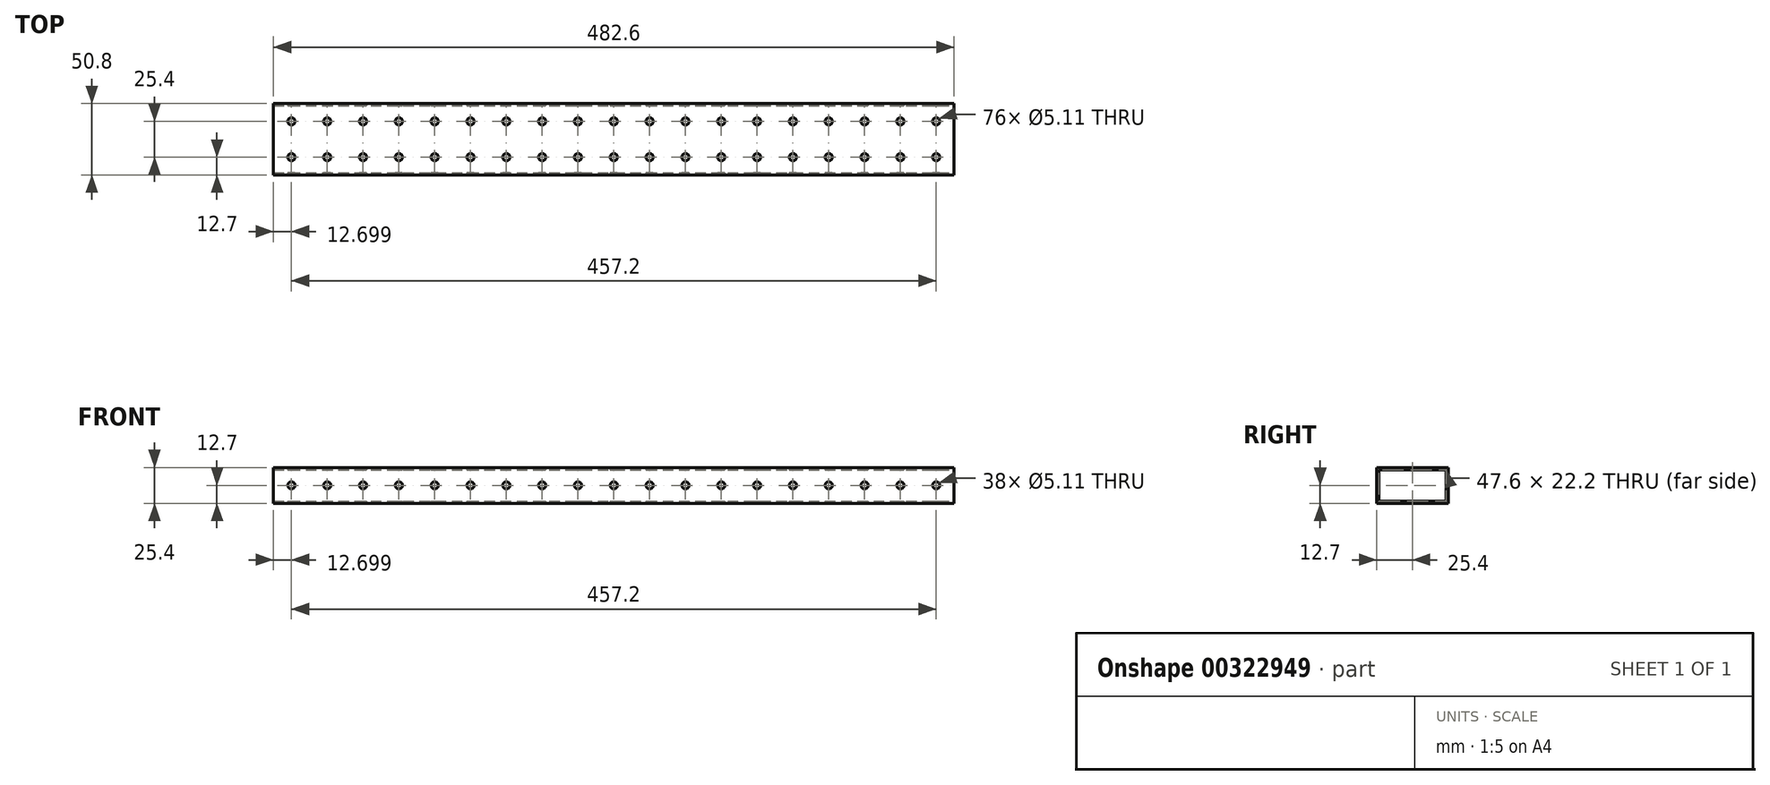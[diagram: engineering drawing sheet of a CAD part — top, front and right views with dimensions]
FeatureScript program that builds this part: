
annotation { "Feature Type Name" : "Feature", "Feature Type Description" : "" }
export const myFeature = defineFeature(function(context is Context, id is Id, definition is map)
    precondition{}
    {
        {
            var Q0;
            Q0=qCreatedBy(makeId("Top.planeOp"),FACE);
            var sketch = newSketch(context, id + "F0", { "sketchPlane" : qUnion([Q0])});
            skLineSegment(sketch, "E0.bottom", {"start": v(-213.03, 43.97) * mm, "end": v(269.57, 43.97) * mm});
            skLineSegment(sketch, "E0.top", {"start": v(-213.03, -6.83) * mm, "end": v(269.57, -6.83) * mm});
            skLineSegment(sketch, "E0.left", {"start": v(-213.03, 43.97) * mm, "end": v(-213.03, -6.83) * mm});
            skLineSegment(sketch, "E0.right", {"start": v(269.57, 43.97) * mm, "end": v(269.57, -6.83) * mm});
            skSolve(sketch);
        }
        {
            var Q0;
            Q0=makeQuery(id+"F0.imprint","IMPRINT",FACE,{"disambiguationData":[TD([[makeQuery(id+"F0.imprint","IMPRINT",EDGE,{"derivedFrom":sQuery(id+"F0.wireOp",EDGE,"E0.bottom")}),-1.0]])]});
            extrude(context, id + "F1", {"entities" : qUnion([Q0]), "depth" : 25.4 * mm});
        }
        {
            var Q0;
            Q0=makeQuery(id+"F1.opExtrude","SWEPT_FACE",FACE,{"disambiguationData":[OSD([sQuery(id+"F0.wireOp",EDGE,"E0.right")])]});
            var sketch = newSketch(context, id + "F2", { "sketchPlane" : qUnion([Q0])});
            skLineSegment(sketch, "E1.bottom", {"start": v(-5.23, 23.8) * mm, "end": v(42.37, 23.8) * mm});
            skLineSegment(sketch, "E1.top", {"start": v(-5.23, 1.6) * mm, "end": v(42.37, 1.6) * mm});
            skLineSegment(sketch, "E1.left", {"start": v(-5.23, 23.8) * mm, "end": v(-5.23, 1.6) * mm});
            skLineSegment(sketch, "E1.right", {"start": v(42.37, 23.8) * mm, "end": v(42.37, 1.6) * mm});
            skSolve(sketch);
        }
        {
            var Q0;
            Q0 = qSketchRegion(id + "F2", true);
            extrude(context, id + "F3", {"entities" : qUnion([Q0]), "operationType" : NewBodyOperationType.REMOVE, "endBound" : BoundingType.THROUGH_ALL, "oppositeDirection" : true, "depth" : 25.4 * mm});
        }
        {
            var Q0;
            Q0=makeQuery(id+"F1.opExtrude","CAP_FACE",FACE,{"disambiguationData":[OSD([sQuery(id+"F0.wireOp",EDGE,"E0.bottom"),sQuery(id+"F0.wireOp",EDGE,"E0.top"),sQuery(id+"F0.wireOp",EDGE,"E0.left"),sQuery(id+"F0.wireOp",EDGE,"E0.right")])],"isStart":false});
            var sketch = newSketch(context, id + "F4", { "sketchPlane" : qUnion([Q0])});
            skCircle(sketch, "E2", {"center": v(-200.33, 31.27) * mm, "radius": 2.55 * mm});
            skCircle(sketch, "E3.0.1.0", {"center": v(-200.33, 5.87) * mm, "radius": 2.55 * mm});
            skCircle(sketch, "E3.1.0.0", {"center": v(-174.93, 31.27) * mm, "radius": 2.55 * mm});
            skCircle(sketch, "E3.1.1.0", {"center": v(-174.93, 5.87) * mm, "radius": 2.55 * mm});
            skCircle(sketch, "E3.2.0.0", {"center": v(-149.53, 31.27) * mm, "radius": 2.55 * mm});
            skCircle(sketch, "E3.2.1.0", {"center": v(-149.53, 5.87) * mm, "radius": 2.55 * mm});
            skCircle(sketch, "E3.3.0.0", {"center": v(-124.13, 31.27) * mm, "radius": 2.55 * mm});
            skCircle(sketch, "E3.3.1.0", {"center": v(-124.13, 5.87) * mm, "radius": 2.55 * mm});
            skCircle(sketch, "E3.4.0.0", {"center": v(-98.73, 31.27) * mm, "radius": 2.55 * mm});
            skCircle(sketch, "E3.4.1.0", {"center": v(-98.73, 5.87) * mm, "radius": 2.55 * mm});
            skCircle(sketch, "E3.5.0.0", {"center": v(-73.33, 31.27) * mm, "radius": 2.55 * mm});
            skCircle(sketch, "E3.5.1.0", {"center": v(-73.33, 5.87) * mm, "radius": 2.55 * mm});
            skCircle(sketch, "E3.6.0.0", {"center": v(-47.93, 31.27) * mm, "radius": 2.55 * mm});
            skCircle(sketch, "E3.6.1.0", {"center": v(-47.93, 5.87) * mm, "radius": 2.55 * mm});
            skCircle(sketch, "E3.7.0.0", {"center": v(-22.53, 31.27) * mm, "radius": 2.55 * mm});
            skCircle(sketch, "E3.7.1.0", {"center": v(-22.53, 5.87) * mm, "radius": 2.55 * mm});
            skCircle(sketch, "E3.8.0.0", {"center": v(2.87, 31.27) * mm, "radius": 2.55 * mm});
            skCircle(sketch, "E3.8.1.0", {"center": v(2.87, 5.87) * mm, "radius": 2.55 * mm});
            skCircle(sketch, "E3.9.0.0", {"center": v(28.27, 31.27) * mm, "radius": 2.55 * mm});
            skCircle(sketch, "E3.9.1.0", {"center": v(28.27, 5.87) * mm, "radius": 2.55 * mm});
            skCircle(sketch, "E3.10.0.0", {"center": v(53.67, 31.27) * mm, "radius": 2.55 * mm});
            skCircle(sketch, "E3.10.1.0", {"center": v(53.67, 5.87) * mm, "radius": 2.55 * mm});
            skCircle(sketch, "E3.11.0.0", {"center": v(79.07, 31.27) * mm, "radius": 2.55 * mm});
            skCircle(sketch, "E3.11.1.0", {"center": v(79.07, 5.87) * mm, "radius": 2.55 * mm});
            skCircle(sketch, "E3.12.0.0", {"center": v(104.47, 31.27) * mm, "radius": 2.55 * mm});
            skCircle(sketch, "E3.12.1.0", {"center": v(104.47, 5.87) * mm, "radius": 2.55 * mm});
            skCircle(sketch, "E3.13.0.0", {"center": v(129.87, 31.27) * mm, "radius": 2.55 * mm});
            skCircle(sketch, "E3.13.1.0", {"center": v(129.87, 5.87) * mm, "radius": 2.55 * mm});
            skCircle(sketch, "E3.14.0.0", {"center": v(155.27, 31.27) * mm, "radius": 2.55 * mm});
            skCircle(sketch, "E3.14.1.0", {"center": v(155.27, 5.87) * mm, "radius": 2.55 * mm});
            skCircle(sketch, "E3.15.0.0", {"center": v(180.67, 31.27) * mm, "radius": 2.55 * mm});
            skCircle(sketch, "E3.15.1.0", {"center": v(180.67, 5.87) * mm, "radius": 2.55 * mm});
            skCircle(sketch, "E3.16.0.0", {"center": v(206.07, 31.27) * mm, "radius": 2.55 * mm});
            skCircle(sketch, "E3.16.1.0", {"center": v(206.07, 5.87) * mm, "radius": 2.55 * mm});
            skCircle(sketch, "E3.17.0.0", {"center": v(231.47, 31.27) * mm, "radius": 2.55 * mm});
            skCircle(sketch, "E3.17.1.0", {"center": v(231.47, 5.87) * mm, "radius": 2.55 * mm});
            skCircle(sketch, "E3.18.0.0", {"center": v(256.87, 31.27) * mm, "radius": 2.55 * mm});
            skCircle(sketch, "E3.18.1.0", {"center": v(256.87, 5.87) * mm, "radius": 2.55 * mm});
            skLineSegment(sketch, "E3.direction1", {"start": v(-200.33, 31.27) * mm, "end": v(-174.93, 31.27) * mm, "construction": true});
            skLineSegment(sketch, "E3.direction2", {"start": v(-200.33, 31.27) * mm, "end": v(-200.33, 5.87) * mm, "construction": true});
            skSolve(sketch);
        }
        {
            var Q0;
            Q0=sQuery(id+"F4.wireOp",VERTEX,"E3.8.1.0.center");
            var Q1;
            Q1=sQuery(id+"F4.wireOp",VERTEX,"E3.6.0.0.center");
            var Q2;
            Q2=sQuery(id+"F4.wireOp",VERTEX,"E3.4.0.0.center");
            var Q3;
            Q3=sQuery(id+"F4.wireOp",VERTEX,"E3.7.1.0.center");
            var Q4;
            Q4=sQuery(id+"F4.wireOp",VERTEX,"E3.3.1.0.center");
            var Q5;
            Q5=sQuery(id+"F4.wireOp",VERTEX,"E3.3.0.0.center");
            var Q6;
            Q6=sQuery(id+"F4.wireOp",VERTEX,"E3.2.1.0.center");
            var Q7;
            Q7=sQuery(id+"F4.wireOp",VERTEX,"E3.8.0.0.center");
            var Q8;
            Q8=sQuery(id+"F4.wireOp",VERTEX,"E3.2.0.0.center");
            var Q9;
            Q9=sQuery(id+"F4.wireOp",VERTEX,"E3.1.1.0.center");
            var Q10;
            Q10=sQuery(id+"F4.wireOp",VERTEX,"E3.1.0.0.center");
            var Q11;
            Q11=sQuery(id+"F4.wireOp",VERTEX,"E3.0.1.0.center");
            var Q12;
            Q12=sQuery(id+"F4.wireOp",VERTEX,"E2.center");
            var Q13;
            Q13=sQuery(id+"F4.wireOp",VERTEX,"E3.5.0.0.center");
            var Q14;
            Q14=sQuery(id+"F4.wireOp",VERTEX,"E3.5.1.0.center");
            var Q15;
            Q15=sQuery(id+"F4.wireOp",VERTEX,"E3.4.1.0.center");
            var Q16;
            Q16=sQuery(id+"F4.wireOp",VERTEX,"E3.7.0.0.center");
            var Q17;
            Q17=sQuery(id+"F4.wireOp",VERTEX,"E3.6.1.0.center");
            var Q18;
            Q18=sQuery(id+"F4.wireOp",VERTEX,"E3.18.0.0.center");
            var Q19;
            Q19=sQuery(id+"F4.wireOp",VERTEX,"E3.16.1.0.center");
            var Q20;
            Q20=sQuery(id+"F4.wireOp",VERTEX,"E3.13.0.0.center");
            var Q21;
            Q21=sQuery(id+"F4.wireOp",VERTEX,"E3.11.1.0.center");
            var Q22;
            Q22=sQuery(id+"F4.wireOp",VERTEX,"E3.14.0.0.center");
            var Q23;
            Q23=sQuery(id+"F4.wireOp",VERTEX,"E3.17.1.0.center");
            var Q24;
            Q24=sQuery(id+"F4.wireOp",VERTEX,"E3.15.1.0.center");
            var Q25;
            Q25=sQuery(id+"F4.wireOp",VERTEX,"E3.9.1.0.center");
            var Q26;
            Q26=sQuery(id+"F4.wireOp",VERTEX,"E3.18.1.0.center");
            var Q27;
            Q27=sQuery(id+"F4.wireOp",VERTEX,"E3.12.1.0.center");
            var Q28;
            Q28=sQuery(id+"F4.wireOp",VERTEX,"E3.10.1.0.center");
            var Q29;
            Q29=sQuery(id+"F4.wireOp",VERTEX,"E3.16.0.0.center");
            var Q30;
            Q30=sQuery(id+"F4.wireOp",VERTEX,"E3.15.0.0.center");
            var Q31;
            Q31=sQuery(id+"F4.wireOp",VERTEX,"E3.9.0.0.center");
            var Q32;
            Q32=sQuery(id+"F4.wireOp",VERTEX,"E3.13.1.0.center");
            var Q33;
            Q33=sQuery(id+"F4.wireOp",VERTEX,"E3.17.0.0.center");
            var Q34;
            Q34=sQuery(id+"F4.wireOp",VERTEX,"E3.10.0.0.center");
            var Q35;
            Q35=sQuery(id+"F4.wireOp",VERTEX,"E3.12.0.0.center");
            var Q36;
            Q36=sQuery(id+"F4.wireOp",VERTEX,"E3.11.0.0.center");
            var Q37;
            Q37=sQuery(id+"F4.wireOp",VERTEX,"E3.14.1.0.center");
            var Q38;
            Q38=makeQuery(id+"F1.opExtrude","SWEPT_BODY",BODY,{"disambiguationData":[OSD([sQuery(id+"F0.wireOp",EDGE,"E0.bottom"),sQuery(id+"F0.wireOp",EDGE,"E0.top"),sQuery(id+"F0.wireOp",EDGE,"E0.left"),sQuery(id+"F0.wireOp",EDGE,"E0.right")])]});
            hole(context, id + "F5", {"style" : HoleStyle.SIMPLE, "endStyle" : HoleEndStyle.THROUGH, "holeDiameter" : 5.1 * mm, "tappedDepth" : 12.7 * mm, "tapClearance" : 3, "locations" : qUnion([Q0, Q1, Q2, Q3, Q4, Q5, Q6, Q7, Q8, Q9, Q10, Q11, Q12, Q13, Q14, Q15, Q16, Q17, Q18, Q19, Q20, Q21, Q22, Q23, Q24, Q25, Q26, Q27, Q28, Q29, Q30, Q31, Q32, Q33, Q34, Q35, Q36, Q37]), "scope" : qUnion([Q38])});
        }
        {
            var Q0;
            Q0=makeQuery(id+"F1.opExtrude","SWEPT_FACE",FACE,{"disambiguationData":[OSD([sQuery(id+"F0.wireOp",EDGE,"E0.bottom")])]});
            var sketch = newSketch(context, id + "F6", { "sketchPlane" : qUnion([Q0])});
            skCircle(sketch, "E4", {"center": v(-256.87, 12.7) * mm, "radius": 2.55 * mm});
            skCircle(sketch, "E5.1.0.0", {"center": v(-231.47, 12.7) * mm, "radius": 2.55 * mm});
            skCircle(sketch, "E5.2.0.0", {"center": v(-206.07, 12.7) * mm, "radius": 2.55 * mm});
            skCircle(sketch, "E5.3.0.0", {"center": v(-180.67, 12.7) * mm, "radius": 2.55 * mm});
            skCircle(sketch, "E5.4.0.0", {"center": v(-155.27, 12.7) * mm, "radius": 2.55 * mm});
            skCircle(sketch, "E5.5.0.0", {"center": v(-129.87, 12.7) * mm, "radius": 2.55 * mm});
            skCircle(sketch, "E5.6.0.0", {"center": v(-104.47, 12.7) * mm, "radius": 2.55 * mm});
            skCircle(sketch, "E5.7.0.0", {"center": v(-79.07, 12.7) * mm, "radius": 2.55 * mm});
            skCircle(sketch, "E5.8.0.0", {"center": v(-53.67, 12.7) * mm, "radius": 2.55 * mm});
            skCircle(sketch, "E5.9.0.0", {"center": v(-28.27, 12.7) * mm, "radius": 2.55 * mm});
            skCircle(sketch, "E5.10.0.0", {"center": v(-2.87, 12.7) * mm, "radius": 2.55 * mm});
            skCircle(sketch, "E5.11.0.0", {"center": v(22.53, 12.7) * mm, "radius": 2.55 * mm});
            skCircle(sketch, "E5.12.0.0", {"center": v(47.93, 12.7) * mm, "radius": 2.55 * mm});
            skCircle(sketch, "E5.13.0.0", {"center": v(73.33, 12.7) * mm, "radius": 2.55 * mm});
            skCircle(sketch, "E5.14.0.0", {"center": v(98.73, 12.7) * mm, "radius": 2.55 * mm});
            skCircle(sketch, "E5.15.0.0", {"center": v(124.13, 12.7) * mm, "radius": 2.55 * mm});
            skCircle(sketch, "E5.16.0.0", {"center": v(149.53, 12.7) * mm, "radius": 2.55 * mm});
            skCircle(sketch, "E5.17.0.0", {"center": v(174.93, 12.7) * mm, "radius": 2.55 * mm});
            skCircle(sketch, "E5.18.0.0", {"center": v(200.33, 12.7) * mm, "radius": 2.55 * mm});
            skLineSegment(sketch, "E5.direction1", {"start": v(-256.87, 12.7) * mm, "end": v(-231.47, 12.7) * mm, "construction": true});
            skSolve(sketch);
        }
        {
            var Q0;
            Q0=sQuery(id+"F6.wireOp",VERTEX,"E5.12.0.0.center");
            var Q1;
            Q1=sQuery(id+"F6.wireOp",VERTEX,"E5.11.0.0.center");
            var Q2;
            Q2=sQuery(id+"F6.wireOp",VERTEX,"E5.13.0.0.center");
            var Q3;
            Q3=sQuery(id+"F6.wireOp",VERTEX,"E5.7.0.0.center");
            var Q4;
            Q4=sQuery(id+"F6.wireOp",VERTEX,"E5.6.0.0.center");
            var Q5;
            Q5=sQuery(id+"F6.wireOp",VERTEX,"E5.9.0.0.center");
            var Q6;
            Q6=sQuery(id+"F6.wireOp",VERTEX,"E5.8.0.0.center");
            var Q7;
            Q7=sQuery(id+"F6.wireOp",VERTEX,"E5.10.0.0.center");
            var Q8;
            Q8=sQuery(id+"F6.wireOp",VERTEX,"E5.16.0.0.center");
            var Q9;
            Q9=sQuery(id+"F6.wireOp",VERTEX,"E5.14.0.0.center");
            var Q10;
            Q10=sQuery(id+"F6.wireOp",VERTEX,"E5.1.0.0.center");
            var Q11;
            Q11=sQuery(id+"F6.wireOp",VERTEX,"E4.center");
            var Q12;
            Q12=sQuery(id+"F6.wireOp",VERTEX,"E5.3.0.0.center");
            var Q13;
            Q13=sQuery(id+"F6.wireOp",VERTEX,"E5.2.0.0.center");
            var Q14;
            Q14=sQuery(id+"F6.wireOp",VERTEX,"E5.4.0.0.center");
            var Q15;
            Q15=sQuery(id+"F6.wireOp",VERTEX,"E5.5.0.0.center");
            var Q16;
            Q16=sQuery(id+"F6.wireOp",VERTEX,"E5.15.0.0.center");
            var Q17;
            Q17=sQuery(id+"F6.wireOp",VERTEX,"E5.18.0.0.center");
            var Q18;
            Q18=sQuery(id+"F6.wireOp",VERTEX,"E5.17.0.0.center");
            var Q19;
            Q19=makeQuery(id+"F1.opExtrude","SWEPT_BODY",BODY,{"disambiguationData":[OSD([sQuery(id+"F0.wireOp",EDGE,"E0.bottom"),sQuery(id+"F0.wireOp",EDGE,"E0.top"),sQuery(id+"F0.wireOp",EDGE,"E0.left"),sQuery(id+"F0.wireOp",EDGE,"E0.right")])]});
            hole(context, id + "F7", {"style" : HoleStyle.SIMPLE, "endStyle" : HoleEndStyle.THROUGH, "holeDiameter" : 5.1 * mm, "tappedDepth" : 12.7 * mm, "tapClearance" : 3, "locations" : qUnion([Q0, Q1, Q2, Q3, Q4, Q5, Q6, Q7, Q8, Q9, Q10, Q11, Q12, Q13, Q14, Q15, Q16, Q17, Q18]), "scope" : qUnion([Q19])});
        }
    });
